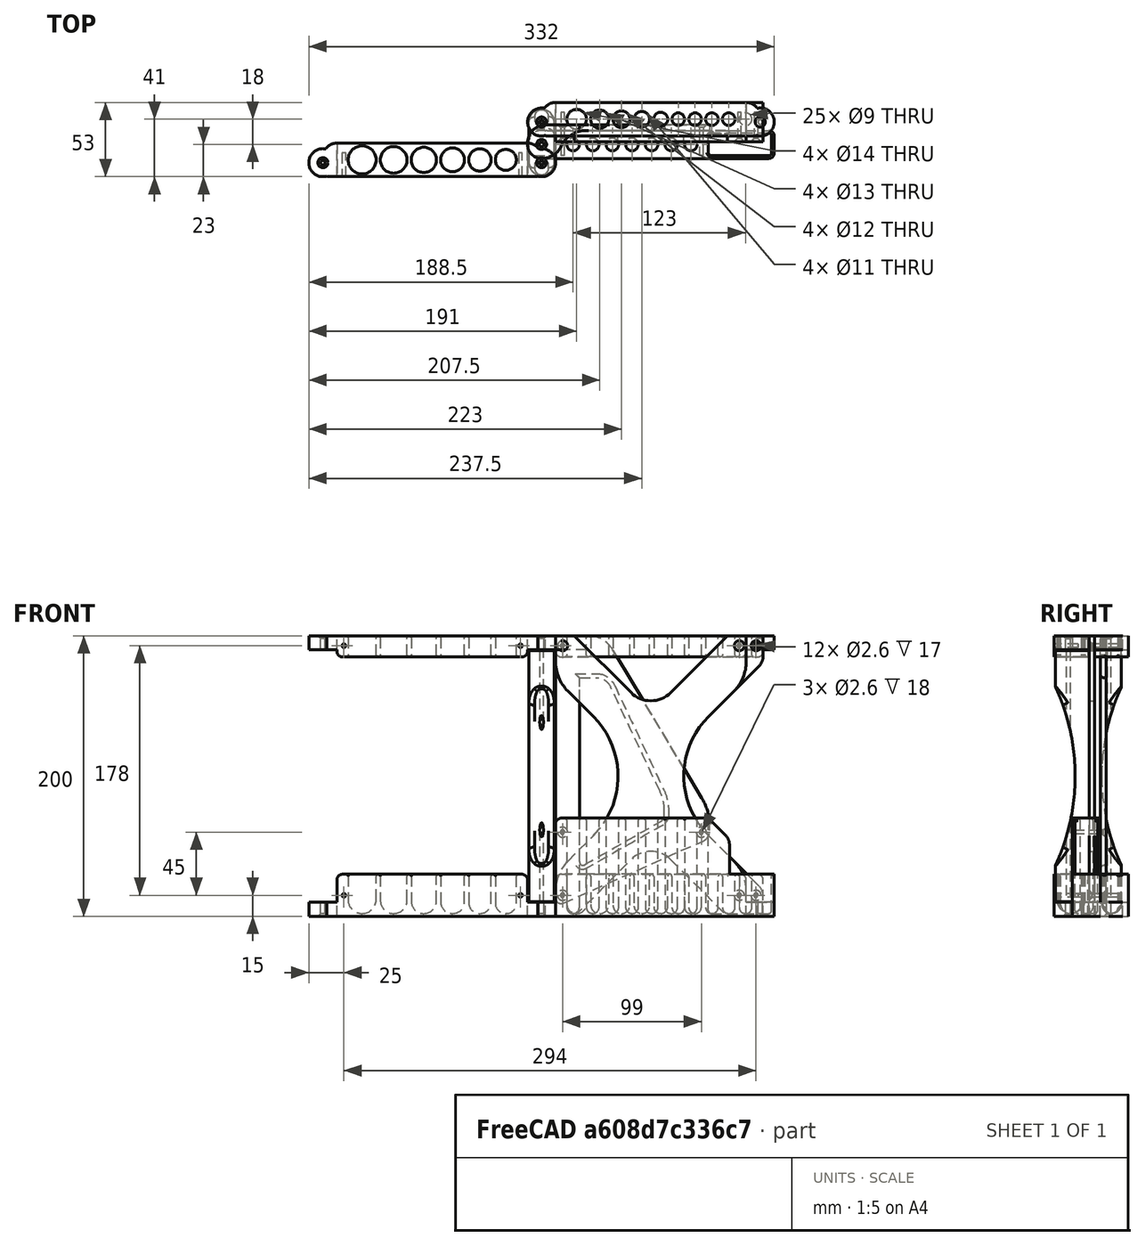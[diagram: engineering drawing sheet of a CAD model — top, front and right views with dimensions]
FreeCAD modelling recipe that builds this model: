
FCSTD DOCUMENT  (FreeCAD 0.21R33771 (Git))
Label: BrushHolder
License: All rights reserved
LicenseURL: https://en.wikipedia.org/wiki/All_rights_reserved
objects: Part::Fillet×106, Part::Cylinder×87, Part::MultiFuse×37, Part::Box×36, Part::Chamfer×24, Part::Cut×17, Part::FeaturePython×12, Part::Feature×1
note: 320 computed .brp shape members not serialized (recipe doc carries the construction recipe); baked Part::Feature solids carry a one-line shape summary decoded from their .brp

FEATURE [Part::Box] Box  label="Cube"
  AttacherType = Attacher::AttachEngine3D
  Height = 30
  Length = 136
  Placement = pos=(-18,-12,0) rot=(0,0,1;0rad)
  Width = 24
FEATURE [Part::Cylinder] Cylinder
  Angle = 360
  AttacherType = Attacher::AttachEngine3D
  FirstAngle = 0
  Height = 30
  Placement = pos=(0,0,2) rot=(0,0,1;0rad)
  Radius = 10
  SecondAngle = 0
FEATURE [Part::Fillet] Fillet
  Base = -> Cylinder
  Edges = 1 edges r=9.9: [Edge2]
FEATURE [Part::Cylinder] Cylinder001
  Angle = 360
  AttacherType = Attacher::AttachEngine3D
  FirstAngle = 0
  Height = 30
  Placement = pos=(22.5,0,2) rot=(0,0,1;0rad)
  Radius = 9.5
  SecondAngle = 0
FEATURE [Part::Fillet] Fillet002
  Base = -> Cylinder001
  Edges = 1 edges r=9.4: [Edge2]
FEATURE [Part::Cylinder] Cylinder002
  Angle = 360
  AttacherType = Attacher::AttachEngine3D
  FirstAngle = 0
  Height = 30
  Placement = pos=(44,0,2) rot=(0,0,1;0rad)
  Radius = 9
  SecondAngle = 0
FEATURE [Part::Fillet] Fillet003
  Base = -> Cylinder002
  Edges = 1 edges r=8.9: [Edge2]
FEATURE [Part::Cylinder] Cylinder003
  Angle = 360
  AttacherType = Attacher::AttachEngine3D
  FirstAngle = 0
  Height = 30
  Placement = pos=(64.5,0,2) rot=(0,0,1;0rad)
  Radius = 8.5
  SecondAngle = 0
FEATURE [Part::Fillet] Fillet004
  Base = -> Cylinder003
  Edges = 1 edges r=8.4: [Edge2]
FEATURE [Part::Cylinder] Cylinder004
  Angle = 360
  AttacherType = Attacher::AttachEngine3D
  FirstAngle = 0
  Height = 30
  Placement = pos=(84,0,2) rot=(0,0,1;0rad)
  Radius = 8
  SecondAngle = 0
FEATURE [Part::Fillet] Fillet005
  Base = -> Cylinder004
  Edges = 1 edges r=7.9: [Edge2]
FEATURE [Part::Cylinder] Cylinder005
  Angle = 360
  AttacherType = Attacher::AttachEngine3D
  FirstAngle = 0
  Height = 30
  Placement = pos=(102.5,0,2) rot=(0,0,1;0rad)
  Radius = 7.5
  SecondAngle = 0
FEATURE [Part::Fillet] Fillet006
  Base = -> Cylinder005
  Edges = 1 edges r=7.4: [Edge2]
FEATURE [Part::MultiFuse] Fusion  label="BrushHolles_001"
  Shapes = -> [Fillet,Fillet002,Fillet003,Fillet004,Fillet005,Fillet006]
FEATURE [Part::Cylinder] Cylinder006
  Angle = 360
  AttacherType = Attacher::AttachEngine3D
  FirstAngle = 0
  Height = 30
  Placement = pos=(-3,0,2) rot=(0,0,1;0rad)
  Radius = 7
  SecondAngle = 0
FEATURE [Part::Fillet] Fillet007
  Base = -> Cylinder006
  Edges = 1 edges r=6.9: [Edge2]
FEATURE [Part::Cylinder] Cylinder007
  Angle = 360
  AttacherType = Attacher::AttachEngine3D
  FirstAngle = 0
  Height = 30
  Placement = pos=(13.5,0,2) rot=(0,0,1;0rad)
  Radius = 6.5
  SecondAngle = 0
FEATURE [Part::Fillet] Fillet008
  Base = -> Cylinder007
  Edges = 1 edges r=6.4: [Edge2]
FEATURE [Part::Cylinder] Cylinder008
  Angle = 360
  AttacherType = Attacher::AttachEngine3D
  FirstAngle = 0
  Height = 30
  Placement = pos=(29,0,2) rot=(0,0,1;0rad)
  Radius = 6
  SecondAngle = 0
FEATURE [Part::Fillet] Fillet009
  Base = -> Cylinder008
  Edges = 1 edges r=5.9: [Edge2]
FEATURE [Part::Cylinder] Cylinder009
  Angle = 360
  AttacherType = Attacher::AttachEngine3D
  FirstAngle = 0
  Height = 30
  Placement = pos=(43.5,0,2) rot=(0,0,1;0rad)
  Radius = 5.5
  SecondAngle = 0
FEATURE [Part::Fillet] Fillet010
  Base = -> Cylinder009
  Edges = 1 edges r=5.4: [Edge2]
FEATURE [Part::Cylinder] Cylinder010
  Angle = 360
  AttacherType = Attacher::AttachEngine3D
  FirstAngle = 0
  Height = 30
  Placement = pos=(57,0,2) rot=(0,0,1;0rad)
  Radius = 5
  SecondAngle = 0
FEATURE [Part::Fillet] Fillet011
  Base = -> Cylinder010
  Edges = 1 edges r=4.9: [Edge2]
FEATURE [Part::Cylinder] Cylinder011
  Angle = 360
  AttacherType = Attacher::AttachEngine3D
  FirstAngle = 0
  Height = 30
  Placement = pos=(69.5,0,2) rot=(0,0,1;0rad)
  Radius = 4.5
  SecondAngle = 0
FEATURE [Part::Fillet] Fillet012
  Base = -> Cylinder011
  Edges = 1 edges r=4.4: [Edge2]
FEATURE [Part::Cylinder] Cylinder012
  Angle = 360
  AttacherType = Attacher::AttachEngine3D
  FirstAngle = 0
  Height = 30
  Placement = pos=(81.5,0,2) rot=(0,0,1;0rad)
  Radius = 4.5
  SecondAngle = 0
FEATURE [Part::Fillet] Fillet013
  Base = -> Cylinder012
  Edges = 1 edges r=4.4: [Edge2]
FEATURE [Part::Cylinder] Cylinder013
  Angle = 360
  AttacherType = Attacher::AttachEngine3D
  FirstAngle = 0
  Height = 30
  Placement = pos=(93.5,0,2) rot=(0,0,1;0rad)
  Radius = 4.5
  SecondAngle = 0
FEATURE [Part::Fillet] Fillet014
  Base = -> Cylinder013
  Edges = 1 edges r=4.4: [Edge2]
FEATURE [Part::Cylinder] Cylinder014
  Angle = 360
  AttacherType = Attacher::AttachEngine3D
  FirstAngle = 0
  Height = 30
  Placement = pos=(105.5,0,2) rot=(0,0,1;0rad)
  Radius = 4.5
  SecondAngle = 0
FEATURE [Part::Fillet] Fillet015
  Base = -> Cylinder014
  Edges = 1 edges r=4.4: [Edge2]
FEATURE [Part::Cut] Cut
  Base = -> Box
  Tool = -> Fusion
FEATURE [Part::Cylinder] Cylinder015  label="ScrewHolle001"
  Angle = 360
  AttacherType = Attacher::AttachEngine3D
  FirstAngle = 0
  Height = 25
  Placement = pos=(-13,-20,15) rot=(-1,0,0;1.5708rad)
  Radius = 1.3
  SecondAngle = 0
FEATURE [Part::MultiFuse] Fusion001  label="BrushHolles_002"
  Shapes = -> [Fillet007,Fillet008,Fillet009,Fillet010,Fillet011,Fillet012,Fillet013,Fillet014,Fillet015]
FEATURE [Part::FeaturePython] Tube  # WARN: FeaturePython — macro-defined, semantics opaque (R4)
  AttacherType = Attacher::AttachEngine3D
  Height = 10
  InnerRadius = 1.6
  OuterRadius = 10
  Placement = pos=(-28,-2,0) rot=(0,0,1;0rad)
FEATURE [Part::Box] Box001  label="Cube001"
  AttacherType = Attacher::AttachEngine3D
  Height = 10
  Length = 10
  Placement = pos=(-26,-12,0) rot=(0,0,1;0rad)
  Width = 24
FEATURE [Part::Fillet] Fillet016
  Base = -> Box001
  Edges = 1 edges r=2: [Edge1]
FEATURE [Part::Chamfer] Chamfer
  Base = -> Fillet016
  Edges = 1 edges r=4: [Edge4]
FEATURE [Part::Fillet] Fillet017
  Base = -> Chamfer
  Edges = 1 edges r=2: [Edge4]
FEATURE [Part::Fillet] Fillet018
  Base = -> Fillet017
  Edges = 1 edges r=10: [Edge19]
FEATURE [Part::FeaturePython] Tube001  # WARN: FeaturePython — macro-defined, semantics opaque (R4)
  AttacherType = Attacher::AttachEngine3D
  Height = 10
  InnerRadius = 1.6
  OuterRadius = 10
  Placement = pos=(128,-2,0) rot=(0,0,1;0rad)
FEATURE [Part::Box] Box002  label="Cube002"
  AttacherType = Attacher::AttachEngine3D
  Height = 10
  Length = 10
  Placement = pos=(116,-12,0) rot=(0,0,1;0rad)
  Width = 24
FEATURE [Part::Fillet] Fillet019
  Base = -> Box002
  Edges = 1 edges r=2: [Edge5]
FEATURE [Part::Chamfer] Chamfer001
  Base = -> Fillet019
  Edges = 1 edges r=4: [Edge4]
FEATURE [Part::Fillet] Fillet020
  Base = -> Chamfer001
  Edges = 1 edges r=2: [Edge4]
FEATURE [Part::Fillet] Fillet021
  Base = -> Fillet020
  Edges = 1 edges r=10: [Edge19]
FEATURE [Part::Fillet] Fillet022
  Base = -> Cut
  Edges = 2 edges r=4: [Edge2,Edge9]
FEATURE [Part::Fillet] Fillet023
  Base = -> Fillet022
  Edges = 6 edges r=1.4: [Edge19,Edge20,Edge21,Edge22,Edge23,Edge24]
FEATURE [Part::MultiFuse] Fusion002  label="Hindges001"
  Shapes = -> [Tube,Fillet018,Fillet021,Tube001]
FEATURE [Part::Cylinder] Cylinder016  label="ScrewHolle002"
  Angle = 360
  AttacherType = Attacher::AttachEngine3D
  FirstAngle = 0
  Height = 25
  Placement = pos=(113,-20,15) rot=(-1,0,0;1.5708rad)
  Radius = 1.3
  SecondAngle = 0
FEATURE [Part::MultiFuse] Fusion003
  Shapes = -> [Cylinder015,Cylinder016]
FEATURE [Part::Cut] Cut001
  Base = -> Fillet023
  Tool = -> Fusion003
FEATURE [Part::Cylinder] Cylinder017  label="ScrewHolle003"
  Angle = 360
  AttacherType = Attacher::AttachEngine3D
  FirstAngle = 0
  Height = 25
  Placement = pos=(-13,-20,15) rot=(-1,0,0;1.5708rad)
  Radius = 1.3
  SecondAngle = 0
FEATURE [Part::Cylinder] Cylinder018  label="ScrewHolle004"
  Angle = 360
  AttacherType = Attacher::AttachEngine3D
  FirstAngle = 0
  Height = 25
  Placement = pos=(113,-20,15) rot=(-1,0,0;1.5708rad)
  Radius = 1.3
  SecondAngle = 0
FEATURE [Part::MultiFuse] Fusion005
  Shapes = -> [Cylinder017,Cylinder018]
FEATURE [Part::Box] Box003  label="Cube003"
  AttacherType = Attacher::AttachEngine3D
  Height = 10
  Length = 10
  Placement = pos=(-26,-12,0) rot=(0,0,1;0rad)
  Width = 24
FEATURE [Part::Box] Box004  label="Cube004"
  AttacherType = Attacher::AttachEngine3D
  Height = 10
  Length = 10
  Placement = pos=(116,-12,0) rot=(0,0,1;0rad)
  Width = 24
FEATURE [Part::Fillet] Fillet024
  Base = -> Box003
  Edges = 1 edges r=2: [Edge1]
FEATURE [Part::Chamfer] Chamfer002
  Base = -> Fillet024
  Edges = 1 edges r=4: [Edge4]
FEATURE [Part::Fillet] Fillet025
  Base = -> Chamfer002
  Edges = 1 edges r=2: [Edge4]
FEATURE [Part::Fillet] Fillet026
  Base = -> Fillet025
  Edges = 1 edges r=10: [Edge19]
FEATURE [Part::Fillet] Fillet027
  Base = -> Box004
  Edges = 1 edges r=2: [Edge5]
FEATURE [Part::Chamfer] Chamfer003
  Base = -> Fillet027
  Edges = 1 edges r=4: [Edge4]
FEATURE [Part::Fillet] Fillet028
  Base = -> Chamfer003
  Edges = 1 edges r=2: [Edge4]
FEATURE [Part::Fillet] Fillet029
  Base = -> Fillet028
  Edges = 1 edges r=10: [Edge19]
FEATURE [Part::FeaturePython] Tube002  # WARN: FeaturePython — macro-defined, semantics opaque (R4)
  AttacherType = Attacher::AttachEngine3D
  Height = 10
  InnerRadius = 1.6
  OuterRadius = 10
  Placement = pos=(-28,-2,0) rot=(0,0,1;0rad)
FEATURE [Part::FeaturePython] Tube003  # WARN: FeaturePython — macro-defined, semantics opaque (R4)
  AttacherType = Attacher::AttachEngine3D
  Height = 10
  InnerRadius = 1.6
  OuterRadius = 10
  Placement = pos=(128,-2,0) rot=(0,0,1;0rad)
FEATURE [Part::MultiFuse] Fusion006  label="Hindges002"
  Shapes = -> [Tube002,Fillet026,Fillet029,Tube003]
FEATURE [Part::Box] Box005  label="Cube005"
  AttacherType = Attacher::AttachEngine3D
  Height = 30
  Length = 136
  Placement = pos=(-18,-12,0) rot=(0,0,1;0rad)
  Width = 24
FEATURE [Part::MultiFuse] Fusion007
  Shapes = -> [Fusion001,Fusion005]
FEATURE [Part::Cut] Cut002
  Base = -> Box005
  Tool = -> Fusion007
FEATURE [Part::Fillet] Fillet030
  Base = -> Cut002
  Edges = 2 edges r=4: [Edge2,Edge11]
FEATURE [Part::Fillet] Fillet031
  Base = -> Fillet030
  Edges = 9 edges r=1.4: [Edge21,Edge22,Edge23,Edge24,Edge25,Edge26,Edge27,Edge28,Edge29]
FEATURE [Part::Cylinder] Cylinder019
  Angle = 360
  AttacherType = Attacher::AttachEngine3D
  FirstAngle = 0
  Height = 30
  Radius = 10
  SecondAngle = 0
FEATURE [Part::Cylinder] Cylinder020
  Angle = 360
  AttacherType = Attacher::AttachEngine3D
  FirstAngle = 0
  Height = 30
  Placement = pos=(22.5,0,0) rot=(0,0,1;0rad)
  Radius = 9.5
  SecondAngle = 0
FEATURE [Part::Cylinder] Cylinder021
  Angle = 360
  AttacherType = Attacher::AttachEngine3D
  FirstAngle = 0
  Height = 30
  Placement = pos=(44,0,0) rot=(0,0,1;0rad)
  Radius = 9
  SecondAngle = 0
FEATURE [Part::Cylinder] Cylinder022
  Angle = 360
  AttacherType = Attacher::AttachEngine3D
  FirstAngle = 0
  Height = 30
  Placement = pos=(64.5,0,0) rot=(0,0,1;0rad)
  Radius = 8.5
  SecondAngle = 0
FEATURE [Part::Cylinder] Cylinder023
  Angle = 360
  AttacherType = Attacher::AttachEngine3D
  FirstAngle = 0
  Height = 30
  Placement = pos=(84,0,0) rot=(0,0,1;0rad)
  Radius = 8
  SecondAngle = 0
FEATURE [Part::Cylinder] Cylinder024
  Angle = 360
  AttacherType = Attacher::AttachEngine3D
  FirstAngle = 0
  Height = 30
  Placement = pos=(102.5,0,0) rot=(0,0,1;0rad)
  Radius = 7.5
  SecondAngle = 0
FEATURE [Part::Box] Box006  label="Cube006"
  AttacherType = Attacher::AttachEngine3D
  Height = 15
  Length = 136
  Placement = pos=(-18,-12,15) rot=(0,0,1;0rad)
  Width = 24
FEATURE [Part::MultiFuse] Fusion009
  Shapes = -> [Cylinder019,Cylinder020,Cylinder021,Cylinder022,Cylinder023,Cylinder024]
FEATURE [Part::Cut] Cut003
  Base = -> Box006
  Tool = -> Fusion009
FEATURE [Part::Box] Box007  label="Cube007"
  AttacherType = Attacher::AttachEngine3D
  Height = 10
  Length = 10
  Placement = pos=(-26,-12,0) rot=(0,0,1;0rad)
  Width = 24
FEATURE [Part::Box] Box008  label="Cube008"
  AttacherType = Attacher::AttachEngine3D
  Height = 10
  Length = 10
  Placement = pos=(116,-12,0) rot=(0,0,1;0rad)
  Width = 24
FEATURE [Part::Fillet] Fillet034
  Base = -> Box007
  Edges = 1 edges r=2: [Edge1]
FEATURE [Part::Chamfer] Chamfer004
  Base = -> Fillet034
  Edges = 1 edges r=4: [Edge4]
FEATURE [Part::Fillet] Fillet035
  Base = -> Chamfer004
  Edges = 1 edges r=2: [Edge4]
FEATURE [Part::Fillet] Fillet036
  Base = -> Fillet035
  Edges = 1 edges r=10: [Edge19]
FEATURE [Part::Fillet] Fillet037
  Base = -> Box008
  Edges = 1 edges r=2: [Edge5]
FEATURE [Part::Chamfer] Chamfer005
  Base = -> Fillet037
  Edges = 1 edges r=4: [Edge4]
FEATURE [Part::Fillet] Fillet038
  Base = -> Chamfer005
  Edges = 1 edges r=2: [Edge4]
FEATURE [Part::Fillet] Fillet039
  Base = -> Fillet038
  Edges = 1 edges r=10: [Edge19]
FEATURE [Part::FeaturePython] Tube004  # WARN: FeaturePython — macro-defined, semantics opaque (R4)
  AttacherType = Attacher::AttachEngine3D
  Height = 10
  InnerRadius = 1.6
  OuterRadius = 10
  Placement = pos=(-28,-2,0) rot=(0,0,1;0rad)
FEATURE [Part::FeaturePython] Tube005  # WARN: FeaturePython — macro-defined, semantics opaque (R4)
  AttacherType = Attacher::AttachEngine3D
  Height = 10
  InnerRadius = 1.6
  OuterRadius = 10
  Placement = pos=(128,-2,0) rot=(0,0,1;0rad)
FEATURE [Part::MultiFuse] Fusion010  label="Hindges003"
  Placement = pos=(0,0,20) rot=(0,0,1;0rad)
  Shapes = -> [Tube004,Fillet036,Fillet039,Tube005]
FEATURE [Part::Fillet] Fillet040
  Base = -> Cut003
  Edges = 2 edges r=4: [Edge4,Edge18]
FEATURE [Part::Fillet] Fillet041
  Base = -> Fillet040
  Edges = 12 edges r=1.4: [Edge14,Edge15,Edge16,Edge17,Edge18,Edge19,Edge24,Edge25,Edge26,Edge27,Edge28,Edge29]
FEATURE [Part::Chamfer] Chamfer006
  Base = -> Fusion010
  Edges = 2 edges r=2: [Edge31,Edge69]
FEATURE [Part::Cylinder] Cylinder025  label="ScrewHolle005"
  Angle = 360
  AttacherType = Attacher::AttachEngine3D
  FirstAngle = 0
  Height = 25
  Placement = pos=(-13,-20,23) rot=(-1,0,0;1.5708rad)
  Radius = 1.3
  SecondAngle = 0
FEATURE [Part::Cylinder] Cylinder026  label="ScrewHolle006"
  Angle = 360
  AttacherType = Attacher::AttachEngine3D
  FirstAngle = 0
  Height = 25
  Placement = pos=(113,-20,23) rot=(-1,0,0;1.5708rad)
  Radius = 1.3
  SecondAngle = 0
FEATURE [Part::MultiFuse] Fusion011
  Shapes = -> [Cylinder025,Cylinder026]
FEATURE [Part::Cut] Cut004
  Base = -> Fillet041
  Tool = -> Fusion011
FEATURE [Part::MultiFuse] Fusion012  label="Top_L"
  Placement = pos=(-156,-13,170) rot=(0,0,1;0rad)
  Shapes = -> [Cut004,Chamfer006]
FEATURE [Part::Chamfer] Chamfer007
  Base = -> Fusion002
  Edges = 2 edges r=2: [Edge14,Edge74]
FEATURE [Part::MultiFuse] Fusion013  label="BrushHolles_L"
  Placement = pos=(-156,-13,0) rot=(0,0,1;0rad)
  Shapes = -> [Chamfer007,Cut001]
FEATURE [Part::Box] Box010  label="Cube010"
  AttacherType = Attacher::AttachEngine3D
  Height = 10
  Length = 42
  Placement = pos=(-38,-12,190) rot=(0,0,1;0rad)
  Width = 24
FEATURE [Part::Chamfer] Chamfer011
  Base = -> Fusion006
  Edges = 2 edges r=2: [Edge14,Edge74]
FEATURE [Part::MultiFuse] Fusion018  label="BrushHolles_S"
  Placement = pos=(0,16,0) rot=(0,0,1;0rad)
  Shapes = -> [Chamfer011,Fillet031]
FEATURE [Part::Cylinder] Cylinder038  label="ScrewHolle009"
  Angle = 360
  AttacherType = Attacher::AttachEngine3D
  FirstAngle = 0
  Height = 25
  Placement = pos=(-13,-20,15) rot=(-1,0,0;1.5708rad)
  Radius = 1.6
  SecondAngle = 0
FEATURE [Part::Cylinder] Cylinder039  label="ScrewHolle010"
  Angle = 360
  AttacherType = Attacher::AttachEngine3D
  FirstAngle = 0
  Height = 25
  Placement = pos=(113,-20,15) rot=(-1,0,0;1.5708rad)
  Radius = 1.6
  SecondAngle = 0
FEATURE [Part::Cylinder] Cylinder040  label="ScrewHolle011"
  Angle = 360
  AttacherType = Attacher::AttachEngine3D
  FirstAngle = 0
  Height = 25
  Placement = pos=(-13,-20,193) rot=(-1,0,0;1.5708rad)
  Radius = 1.6
  SecondAngle = 0
FEATURE [Part::Cylinder] Cylinder041  label="ScrewHolle012"
  Angle = 360
  AttacherType = Attacher::AttachEngine3D
  FirstAngle = 0
  Height = 25
  Placement = pos=(113,-20,193) rot=(-1,0,0;1.5708rad)
  Radius = 1.6
  SecondAngle = 0
FEATURE [Part::MultiFuse] Fusion019  label="ScrewHolles"
  Shapes = -> [Cylinder038,Cylinder039,Cylinder040,Cylinder041]
FEATURE [Part::Box] Box013  label="Cube013"
  AttacherType = Attacher::AttachEngine3D
  Height = 80
  Length = 80
  Placement = pos=(-6.57,0,202) rot=(0,1,0;0.785398rad)
  Width = 4
FEATURE [Part::Box] Box014  label="Cube014"
  AttacherType = Attacher::AttachEngine3D
  Height = 100
  Length = 100
  Placement = pos=(-90,0,100) rot=(0,1,0;0.785398rad)
  Width = 4
FEATURE [Part::Box] Box015  label="Cube015"
  AttacherType = Attacher::AttachEngine3D
  Height = 179.2
  Length = 18
  Placement = pos=(-37,-24,10.4) rot=(0,0,1;0rad)
  Width = 47
FEATURE [Part::Fillet] Fillet054
  Base = -> Box015
  Edges = 4 edges r=8.9: [Edge1,Edge3,Edge5,Edge7]
FEATURE [Part::Cylinder] Cylinder042
  Angle = 360
  AttacherType = Attacher::AttachEngine3D
  FirstAngle = 0
  Height = 190
  Placement = pos=(-28,14,10) rot=(0,0,1;0rad)
  Radius = 1.3
  SecondAngle = 0
FEATURE [Part::Cylinder] Cylinder043
  Angle = 360
  AttacherType = Attacher::AttachEngine3D
  FirstAngle = 0
  Height = 190
  Placement = pos=(-28,-15,10) rot=(0,0,1;0rad)
  Radius = 1.3
  SecondAngle = 0
FEATURE [Part::Box] Box016  label="Cube016"
  AttacherType = Attacher::AttachEngine3D
  Height = 140
  Length = 20
  Placement = pos=(-38,0,30) rot=(0,0,1;0rad)
  Width = 47
FEATURE [Part::Chamfer] Chamfer015
  Base = -> Box016
  Edges = 2 edges r=20: [Edge11,Edge12]
FEATURE [Part::Chamfer] Chamfer016
  Base = -> Chamfer015
  Edges = 2 edges r=20: [Edge10,Edge15]
FEATURE [Part::Fillet] Fillet055
  Base = -> Chamfer016
  Edges = 2 edges r=20: [Edge9,Edge20]
FEATURE [Part::Fillet] Fillet056
  Base = -> Fillet055
  Edges = 2 edges r=8: [Edge13,Edge25]
FEATURE [Part::Fillet] Fillet057  label="Hollow005"
  Base = -> Fillet056
  Edges = 2 edges r=150: [Edge22,Edge27]
  Placement = pos=(0,-57,0) rot=(0,0,1;0rad)
FEATURE [Part::Feature] Part__Mirroring003  label="Hollow006"
  Placement = pos=(0,2,0) rot=(0,0,1;0rad)
  shape: bbox 20 x 47 x 140 mm, 16 faces (baked)
FEATURE [Part::MultiFuse] Fusion021
  Shapes = -> [Part__Mirroring003,Fillet057,Cylinder043,Cylinder042]
FEATURE [Part::Cut] Cut007
  Base = -> Fillet054
  Tool = -> Fusion021
FEATURE [Part::Fillet] Fillet058  label="MainHindge"
  Base = -> Cut007
  Edges = 2 edges r=4: [Edge3,Edge11]
FEATURE [Part::Fillet] Fillet059
  Base = -> Box013
  Edges = 1 edges r=20: [Edge8]
FEATURE [Part::Box] Box017  label="Cube017"
  AttacherType = Attacher::AttachEngine3D
  Height = 80
  Length = 80
  Placement = pos=(-6.57,0,-2) rot=(0,1,0;0.785398rad)
  Width = 4
FEATURE [Part::Fillet] Fillet060
  Base = -> Box017
  Edges = 1 edges r=20: [Edge2]
FEATURE [Part::Box] Box012  label="SupportBase"
  AttacherType = Attacher::AttachEngine3D
  Height = 200
  Length = 136
  Placement = pos=(-18,0,0) rot=(0,0,1;0rad)
  Width = 4
FEATURE [Part::Fillet] Fillet061
  Base = -> Box014
  Edges = 1 edges r=60: [Edge6]
FEATURE [Part::Box] Box018  label="Cube018"
  AttacherType = Attacher::AttachEngine3D
  Height = 100
  Length = 100
  Placement = pos=(48.67,0,100) rot=(0,1,0;0.785398rad)
  Width = 4
FEATURE [Part::Fillet] Fillet062
  Base = -> Box018
  Edges = 1 edges r=60: [Edge4]
FEATURE [Part::MultiFuse] Fusion023
  Shapes = -> [Fillet061,Fillet059,Fillet060,Fillet062,Fusion019]
FEATURE [Part::Cut] Cut008
  Base = -> Box012
  Tool = -> Fusion023
FEATURE [Part::Fillet] Fillet063
  Base = -> Cut008
  Edges = 4 edges r=30: [Edge2,Edge57,Edge60,Edge67]
FEATURE [Part::Chamfer] Chamfer017  label="Support"
  Base = -> Fillet063
  Edges = 4 edges r=2: [Edge28,Edge29,Edge30,Edge31]
FEATURE [Part::Box] Box019  label="Cube019"
  AttacherType = Attacher::AttachEngine3D
  Height = 10
  Length = 10
  Placement = pos=(-26,-12,0) rot=(0,0,1;0rad)
  Width = 20
FEATURE [Part::Box] Box021  label="Cube021"
  AttacherType = Attacher::AttachEngine3D
  Height = 30
  Length = 88
  Placement = pos=(50,-12,0) rot=(0,0,1;0rad)
  Width = 20
FEATURE [Part::Cylinder] Cylinder049 .. Cylinder052  x4 (patterned run collapsed; names and placements below)
  Angle = 360
  AttacherType = Attacher::AttachEngine3D
  FirstAngle = 0
  Height = 120
  Radius = 4.5
  SecondAngle = 0
  placements: 4 in arithmetic series — first pos=(8.5,-2,2) rot=(0,0,1;0rad), step (14,0,0), last pos=(50.5,-2,2) rot=(0,0,1;0rad)
FEATURE [Part::Cylinder] Cylinder053  label="ScrewHolle013"
  Angle = 360
  AttacherType = Attacher::AttachEngine3D
  FirstAngle = 0
  Height = 25
  Placement = pos=(-13,-10,15) rot=(-1,0,0;1.5708rad)
  Radius = 1.3
  SecondAngle = 0
FEATURE [Part::Cylinder] Cylinder054  label="ScrewHolle014"
  Angle = 360
  AttacherType = Attacher::AttachEngine3D
  FirstAngle = 0
  Height = 25
  Placement = pos=(86,-10,60) rot=(-1,0,0;1.5708rad)
  Radius = 1.3
  SecondAngle = 0
FEATURE [Part::Fillet] Fillet069
  Base = -> Cylinder049
  Edges = 1 edges r=4.4: [Edge2]
FEATURE [Part::Fillet] Fillet070
  Base = -> Cylinder050
  Edges = 1 edges r=4.4: [Edge2]
FEATURE [Part::Fillet] Fillet071
  Base = -> Cylinder051
  Edges = 1 edges r=4.4: [Edge2]
FEATURE [Part::Fillet] Fillet072
  Base = -> Cylinder052
  Edges = 1 edges r=4.4: [Edge2]
FEATURE [Part::Fillet] Fillet073
  Base = -> Box019
  Edges = 2 edges r=2: [Edge1,Edge3]
FEATURE [Part::FeaturePython] Tube008  # WARN: FeaturePython — macro-defined, semantics opaque (R4)
  AttacherType = Attacher::AttachEngine3D
  Height = 10
  InnerRadius = 1.6
  OuterRadius = 10
  Placement = pos=(-28,-2,0) rot=(0,0,1;0rad)
FEATURE [Part::Cylinder] Cylinder055
  Angle = 360
  AttacherType = Attacher::AttachEngine3D
  FirstAngle = 0
  Height = 120
  Placement = pos=(-5.5,-2,2) rot=(0,0,1;0rad)
  Radius = 4.5
  SecondAngle = 0
FEATURE [Part::Fillet] Fillet079
  Base = -> Cylinder055
  Edges = 1 edges r=4.4: [Edge2]
FEATURE [Part::Box] Box022  label="Cube022"
  AttacherType = Attacher::AttachEngine3D
  Height = 120
  Length = 45
  Placement = pos=(91,-10,2) rot=(0,0,1;0rad)
  Width = 16
FEATURE [Part::Fillet] Fillet081
  Base = -> Box022
  Edges = 4 edges r=2: [Edge1,Edge3,Edge5,Edge7]
FEATURE [Part::Fillet] Fillet082
  Base = -> Fillet081
  Edges = 1 edges r=2: [Edge16]
FEATURE [Part::Box] Box024  label="Cube024"
  AttacherType = Attacher::AttachEngine3D
  Height = 70
  Length = 124
  Placement = pos=(-18,-12,0) rot=(0,0,1;0rad)
  Width = 20
FEATURE [Part::Fillet] Fillet085
  Base = -> Box021
  Edges = 2 edges r=4: [Edge5,Edge7]
FEATURE [Part::Cylinder] Cylinder056
  Angle = 360
  AttacherType = Attacher::AttachEngine3D
  FirstAngle = 0
  Height = 10
  Placement = pos=(-28,-2,190) rot=(0,0,1;0rad)
  Radius = 1.6
  SecondAngle = 0
FEATURE [Part::Box] Box025  label="Cube025"
  AttacherType = Attacher::AttachEngine3D
  Height = 200
  Length = 110
  Placement = pos=(-18,8,0) rot=(0,0,1;0rad)
  Width = 4
FEATURE [Part::Cylinder] Cylinder060  label="ScrewHolle018"
  Angle = 360
  AttacherType = Attacher::AttachEngine3D
  FirstAngle = 0
  Height = 25
  Placement = pos=(-13,-10,60) rot=(-1,0,0;1.5708rad)
  Radius = 1.3
  SecondAngle = 0
FEATURE [Part::MultiFuse] Fusion035
  Shapes = -> [Fillet073,Tube008]
FEATURE [Part::Chamfer] Chamfer026
  Base = -> Fusion035
  Edges = 1 edges r=2: [Edge17]
FEATURE [Part::Cylinder] Cylinder061  label="ScrewHolle019"
  Angle = 360
  AttacherType = Attacher::AttachEngine3D
  FirstAngle = 0
  Height = 25
  Placement = pos=(-13,-10,15) rot=(-1,0,0;1.5708rad)
  Radius = 1.6
  SecondAngle = 0
FEATURE [Part::Cylinder] Cylinder062  label="ScrewHolle020"
  Angle = 360
  AttacherType = Attacher::AttachEngine3D
  FirstAngle = 0
  Height = 25
  Placement = pos=(-13,-10,60) rot=(-1,0,0;1.5708rad)
  Radius = 1.6
  SecondAngle = 0
FEATURE [Part::Cylinder] Cylinder063  label="ScrewHolle021"
  Angle = 360
  AttacherType = Attacher::AttachEngine3D
  FirstAngle = 0
  Height = 25
  Placement = pos=(86,-10,60) rot=(-1,0,0;1.5708rad)
  Radius = 1.6
  SecondAngle = 0
FEATURE [Part::Cylinder] Cylinder064
  Angle = 360
  AttacherType = Attacher::AttachEngine3D
  FirstAngle = 0
  Height = 10
  Placement = pos=(4,-12,190) rot=(0,0,1;0rad)
  Radius = 20
  SecondAngle = 0
FEATURE [Part::Box] Box026  label="Cube026"
  AttacherType = Attacher::AttachEngine3D
  Height = 10
  Length = 10
  Placement = pos=(-26,-12,0) rot=(0,0,1;0rad)
  Width = 24
FEATURE [Part::Box] Box028  label="Cube028"
  AttacherType = Attacher::AttachEngine3D
  Height = 30
  Length = 148
  Placement = pos=(-18,-12,0) rot=(0,0,1;0rad)
  Width = 24
FEATURE [Part::Cylinder] Cylinder065
  Angle = 360
  AttacherType = Attacher::AttachEngine3D
  FirstAngle = 0
  Height = 30
  Placement = pos=(-3,0,2) rot=(0,0,1;0rad)
  Radius = 7
  SecondAngle = 0
FEATURE [Part::Cylinder] Cylinder066
  Angle = 360
  AttacherType = Attacher::AttachEngine3D
  FirstAngle = 0
  Height = 30
  Placement = pos=(13.5,0,2) rot=(0,0,1;0rad)
  Radius = 6.5
  SecondAngle = 0
FEATURE [Part::Cylinder] Cylinder067
  Angle = 360
  AttacherType = Attacher::AttachEngine3D
  FirstAngle = 0
  Height = 30
  Placement = pos=(29,0,2) rot=(0,0,1;0rad)
  Radius = 6
  SecondAngle = 0
FEATURE [Part::Cylinder] Cylinder068
  Angle = 360
  AttacherType = Attacher::AttachEngine3D
  FirstAngle = 0
  Height = 30
  Placement = pos=(43.5,0,2) rot=(0,0,1;0rad)
  Radius = 5.5
  SecondAngle = 0
FEATURE [Part::Cylinder] Cylinder069
  Angle = 360
  AttacherType = Attacher::AttachEngine3D
  FirstAngle = 0
  Height = 30
  Placement = pos=(57,0,2) rot=(0,0,1;0rad)
  Radius = 5
  SecondAngle = 0
FEATURE [Part::Cylinder] Cylinder070 .. Cylinder073  x4 (patterned run collapsed; names and placements below)
  Angle = 360
  AttacherType = Attacher::AttachEngine3D
  FirstAngle = 0
  Height = 30
  Radius = 4.5
  SecondAngle = 0
  placements: 4 in arithmetic series — first pos=(69.5,0,2) rot=(0,0,1;0rad), step (12,0,0), last pos=(105.5,0,2) rot=(0,0,1;0rad)
FEATURE [Part::Cylinder] Cylinder074  label="ScrewHolle022"
  Angle = 360
  AttacherType = Attacher::AttachEngine3D
  FirstAngle = 0
  Height = 25
  Placement = pos=(-13,-20,15) rot=(-1,0,0;1.5708rad)
  Radius = 1.3
  SecondAngle = 0
FEATURE [Part::Cylinder] Cylinder075  label="ScrewHolle023"
  Angle = 360
  AttacherType = Attacher::AttachEngine3D
  FirstAngle = 0
  Height = 25
  Placement = pos=(125,-20,15) rot=(-1,0,0;1.5708rad)
  Radius = 1.3
  SecondAngle = 0
FEATURE [Part::Fillet] Fillet109  label="Fillet110"
  Base = -> Cylinder065
  Edges = 1 edges r=6.9: [Edge2]
FEATURE [Part::Fillet] Fillet110  label="Fillet111"
  Base = -> Cylinder066
  Edges = 1 edges r=6.4: [Edge2]
FEATURE [Part::Fillet] Fillet111  label="Fillet112"
  Base = -> Cylinder067
  Edges = 1 edges r=5.9: [Edge2]
FEATURE [Part::Fillet] Fillet112  label="Fillet113"
  Base = -> Cylinder068
  Edges = 1 edges r=5.4: [Edge2]
FEATURE [Part::Fillet] Fillet113  label="Fillet114"
  Base = -> Cylinder069
  Edges = 1 edges r=4.9: [Edge2]
FEATURE [Part::Fillet] Fillet114  label="Fillet115"
  Base = -> Cylinder070
  Edges = 1 edges r=4.4: [Edge2]
FEATURE [Part::Fillet] Fillet115  label="Fillet116"
  Base = -> Cylinder071
  Edges = 1 edges r=4.4: [Edge2]
FEATURE [Part::Fillet] Fillet116  label="Fillet117"
  Base = -> Cylinder072
  Edges = 1 edges r=4.4: [Edge2]
FEATURE [Part::Fillet] Fillet117  label="Fillet118"
  Base = -> Cylinder073
  Edges = 1 edges r=4.4: [Edge2]
FEATURE [Part::Fillet] Fillet118  label="Fillet119"
  Base = -> Box026
  Edges = 1 edges r=2: [Edge1]
FEATURE [Part::MultiFuse] Fusion043
  Shapes = -> [Cylinder074,Cylinder075]
FEATURE [Part::FeaturePython] Tube009  # WARN: FeaturePython — macro-defined, semantics opaque (R4)
  AttacherType = Attacher::AttachEngine3D
  Height = 10
  InnerRadius = 1.6
  OuterRadius = 10
  Placement = pos=(-28,-2,0) rot=(0,0,1;0rad)
FEATURE [Part::Cylinder] Cylinder076
  Angle = 360
  AttacherType = Attacher::AttachEngine3D
  FirstAngle = 0
  Height = 30
  Placement = pos=(117.5,0,2) rot=(0,0,1;0rad)
  Radius = 4.5
  SecondAngle = 0
FEATURE [Part::Fillet] Fillet122  label="Fillet123"
  Base = -> Cylinder076
  Edges = 1 edges r=4.4: [Edge2]
FEATURE [Part::Fillet] Fillet123  label="Fillet124"
  Base = -> Box028
  Edges = 2 edges r=4: [Edge2,Edge6]
FEATURE [Part::MultiFuse] Fusion047
  Shapes = -> [Fillet122,Fillet117,Fillet116,Fillet115,Fillet114,Fillet113,Fillet112,Fillet111,Fillet110,Fillet109,Fusion043]
FEATURE [Part::Cut] Cut015
  Base = -> Fillet123
  Tool = -> Fusion047
FEATURE [Part::Fillet] Fillet124  label="Fillet125"
  Base = -> Cut015
  Edges = 10 edges r=1.4: [Edge21,Edge22,Edge23,Edge24,Edge25,Edge26,Edge27,Edge28,Edge29,Edge30]
FEATURE [Part::Chamfer] Chamfer031
  Base = -> Fillet118
  Edges = 1 edges r=4: [Edge4]
FEATURE [Part::Fillet] Fillet119  label="Fillet120"
  Base = -> Chamfer031
  Edges = 1 edges r=2: [Edge4]
FEATURE [Part::Fillet] Fillet120  label="Fillet121"
  Base = -> Fillet119
  Edges = 1 edges r=10: [Edge19]
FEATURE [Part::MultiFuse] Fusion046
  Shapes = -> [Fillet120,Tube009]
FEATURE [Part::Chamfer] Chamfer032
  Base = -> Fusion046
  Edges = 1 edges r=2: [Edge36]
FEATURE [Part::MultiFuse] Fusion048  label="BrushHolles_S2"
  Placement = pos=(0,16,0) rot=(0,0,1;0rad)
  Shapes = -> [Fillet124,Chamfer032]
FEATURE [Part::Box] Box009  label="Cube009"
  AttacherType = Attacher::AttachEngine3D
  Height = 15
  Length = 136
  Placement = pos=(-18,-12,15) rot=(0,0,1;0rad)
  Width = 24
FEATURE [Part::Box] Box029  label="Cube029"
  AttacherType = Attacher::AttachEngine3D
  Height = 10
  Length = 10
  Placement = pos=(-26,-12,0) rot=(0,0,1;0rad)
  Width = 24
FEATURE [Part::Box] Box011  label="Cube011"
  AttacherType = Attacher::AttachEngine3D
  Height = 10
  Length = 10
  Placement = pos=(116,-12,0) rot=(0,0,1;0rad)
  Width = 24
FEATURE [Part::Cylinder] Cylinder027
  Angle = 360
  AttacherType = Attacher::AttachEngine3D
  FirstAngle = 0
  Height = 30
  Placement = pos=(-3,0,0) rot=(0,0,1;0rad)
  Radius = 7
  SecondAngle = 0
FEATURE [Part::Cylinder] Cylinder028
  Angle = 360
  AttacherType = Attacher::AttachEngine3D
  FirstAngle = 0
  Height = 30
  Placement = pos=(13.5,0,0) rot=(0,0,1;0rad)
  Radius = 6.5
  SecondAngle = 0
FEATURE [Part::Cylinder] Cylinder029
  Angle = 360
  AttacherType = Attacher::AttachEngine3D
  FirstAngle = 0
  Height = 30
  Placement = pos=(29,0,0) rot=(0,0,1;0rad)
  Radius = 6
  SecondAngle = 0
FEATURE [Part::Cylinder] Cylinder030
  Angle = 360
  AttacherType = Attacher::AttachEngine3D
  FirstAngle = 0
  Height = 30
  Placement = pos=(43.5,0,0) rot=(0,0,1;0rad)
  Radius = 5.5
  SecondAngle = 0
FEATURE [Part::Cylinder] Cylinder031
  Angle = 360
  AttacherType = Attacher::AttachEngine3D
  FirstAngle = 0
  Height = 30
  Placement = pos=(57,0,0) rot=(0,0,1;0rad)
  Radius = 5
  SecondAngle = 0
FEATURE [Part::Cylinder] Cylinder032 .. Cylinder035  x4 (patterned run collapsed; names and placements below)
  Angle = 360
  AttacherType = Attacher::AttachEngine3D
  FirstAngle = 0
  Height = 30
  Radius = 4.5
  SecondAngle = 0
  placements: 4 in arithmetic series — first pos=(69.5,0,0) rot=(0,0,1;0rad), step (12,0,0), last pos=(105.5,0,0) rot=(0,0,1;0rad)
FEATURE [Part::Cylinder] Cylinder036  label="ScrewHolle007"
  Angle = 360
  AttacherType = Attacher::AttachEngine3D
  FirstAngle = 0
  Height = 25
  Placement = pos=(-13,-20,23) rot=(-1,0,0;1.5708rad)
  Radius = 1.3
  SecondAngle = 0
FEATURE [Part::Cylinder] Cylinder037  label="ScrewHolle008"
  Angle = 360
  AttacherType = Attacher::AttachEngine3D
  FirstAngle = 0
  Height = 25
  Placement = pos=(113,-20,23) rot=(-1,0,0;1.5708rad)
  Radius = 1.3
  SecondAngle = 0
FEATURE [Part::Fillet] Fillet042
  Base = -> Box029
  Edges = 1 edges r=2: [Edge1]
FEATURE [Part::Chamfer] Chamfer008
  Base = -> Fillet042
  Edges = 1 edges r=4: [Edge4]
FEATURE [Part::Fillet] Fillet043
  Base = -> Chamfer008
  Edges = 1 edges r=2: [Edge4]
FEATURE [Part::Fillet] Fillet044
  Base = -> Fillet043
  Edges = 1 edges r=10: [Edge19]
FEATURE [Part::Fillet] Fillet045
  Base = -> Box011
  Edges = 1 edges r=2: [Edge5]
FEATURE [Part::Chamfer] Chamfer009
  Base = -> Fillet045
  Edges = 1 edges r=4: [Edge4]
FEATURE [Part::Fillet] Fillet046
  Base = -> Chamfer009
  Edges = 1 edges r=2: [Edge4]
FEATURE [Part::Fillet] Fillet047
  Base = -> Fillet046
  Edges = 1 edges r=10: [Edge19]
FEATURE [Part::MultiFuse] Fusion015
  Shapes = -> [Cylinder036,Cylinder037]
FEATURE [Part::MultiFuse] Fusion016
  Shapes = -> [Cylinder027,Cylinder028,Cylinder029,Cylinder030,Cylinder031,Cylinder032,Cylinder033,Cylinder034,Cylinder035,Fusion015]
FEATURE [Part::Cut] Cut005
  Base = -> Box009
  Tool = -> Fusion016
FEATURE [Part::Fillet] Fillet048
  Base = -> Cut005
  Edges = 2 edges r=4: [Edge4,Edge23]
FEATURE [Part::Fillet] Fillet049
  Base = -> Fillet048
  Edges = 18 edges r=1.4: [Edge16,Edge17,Edge18,Edge19,Edge20,Edge21,Edge22,Edge23,Edge24,Edge29,Edge30,Edge31,Edge32,Edge33,Edge34,Edge35,Edge36,Edge37]
FEATURE [Part::FeaturePython] Tube006  # WARN: FeaturePython — macro-defined, semantics opaque (R4)
  AttacherType = Attacher::AttachEngine3D
  Height = 10
  InnerRadius = 1.6
  OuterRadius = 10
  Placement = pos=(-28,-2,0) rot=(0,0,1;0rad)
FEATURE [Part::FeaturePython] Tube007  # WARN: FeaturePython — macro-defined, semantics opaque (R4)
  AttacherType = Attacher::AttachEngine3D
  Height = 10
  InnerRadius = 1.6
  OuterRadius = 10
  Placement = pos=(128,-2,0) rot=(0,0,1;0rad)
FEATURE [Part::MultiFuse] Fusion014  label="Hindges004"
  Placement = pos=(0,0,20) rot=(0,0,1;0rad)
  Shapes = -> [Tube006,Fillet044,Fillet047,Tube007]
FEATURE [Part::Chamfer] Chamfer010
  Base = -> Fusion014
  Edges = 2 edges r=2: [Edge31,Edge69]
FEATURE [Part::MultiFuse] Fusion022  label="Top_S"
  Placement = pos=(0,16,170) rot=(0,0,1;0rad)
  Shapes = -> [Fillet049,Chamfer010]
FEATURE [Part::Box] Box030  label="Cube030"
  AttacherType = Attacher::AttachEngine3D
  Height = 15
  Length = 148
  Placement = pos=(-18,-12,15) rot=(0,0,1;0rad)
  Width = 24
FEATURE [Part::Box] Box031  label="Cube031"
  AttacherType = Attacher::AttachEngine3D
  Height = 10
  Length = 10
  Placement = pos=(-26,-12,20) rot=(0,0,1;0rad)
  Width = 24
FEATURE [Part::Cylinder] Cylinder077
  Angle = 360
  AttacherType = Attacher::AttachEngine3D
  FirstAngle = 0
  Height = 30
  Placement = pos=(-3,0,0) rot=(0,0,1;0rad)
  Radius = 7
  SecondAngle = 0
FEATURE [Part::Cylinder] Cylinder078
  Angle = 360
  AttacherType = Attacher::AttachEngine3D
  FirstAngle = 0
  Height = 30
  Placement = pos=(13.5,0,0) rot=(0,0,1;0rad)
  Radius = 6.5
  SecondAngle = 0
FEATURE [Part::Cylinder] Cylinder079
  Angle = 360
  AttacherType = Attacher::AttachEngine3D
  FirstAngle = 0
  Height = 30
  Placement = pos=(29,0,0) rot=(0,0,1;0rad)
  Radius = 6
  SecondAngle = 0
FEATURE [Part::Cylinder] Cylinder080
  Angle = 360
  AttacherType = Attacher::AttachEngine3D
  FirstAngle = 0
  Height = 30
  Placement = pos=(43.5,0,0) rot=(0,0,1;0rad)
  Radius = 5.5
  SecondAngle = 0
FEATURE [Part::Cylinder] Cylinder081
  Angle = 360
  AttacherType = Attacher::AttachEngine3D
  FirstAngle = 0
  Height = 30
  Placement = pos=(57,0,0) rot=(0,0,1;0rad)
  Radius = 5
  SecondAngle = 0
FEATURE [Part::Cylinder] Cylinder082 .. Cylinder085  x4 (patterned run collapsed; names and placements below)
  Angle = 360
  AttacherType = Attacher::AttachEngine3D
  FirstAngle = 0
  Height = 30
  Radius = 4.5
  SecondAngle = 0
  placements: 4 in arithmetic series — first pos=(69.5,0,0) rot=(0,0,1;0rad), step (12,0,0), last pos=(105.5,0,0) rot=(0,0,1;0rad)
FEATURE [Part::Cylinder] Cylinder086  label="ScrewHolle024"
  Angle = 360
  AttacherType = Attacher::AttachEngine3D
  FirstAngle = 0
  Height = 25
  Placement = pos=(-13,-20,23) rot=(-1,0,0;1.5708rad)
  Radius = 1.3
  SecondAngle = 0
FEATURE [Part::Cylinder] Cylinder087  label="ScrewHolle025"
  Angle = 360
  AttacherType = Attacher::AttachEngine3D
  FirstAngle = 0
  Height = 25
  Placement = pos=(125,-20,23) rot=(-1,0,0;1.5708rad)
  Radius = 1.3
  SecondAngle = 0
FEATURE [Part::Fillet] Fillet125  label="Fillet126"
  Base = -> Box031
  Edges = 1 edges r=2: [Edge1]
FEATURE [Part::Chamfer] Chamfer033
  Base = -> Fillet125
  Edges = 1 edges r=4: [Edge4]
FEATURE [Part::Fillet] Fillet126  label="Fillet127"
  Base = -> Chamfer033
  Edges = 1 edges r=2: [Edge4]
FEATURE [Part::Fillet] Fillet127  label="Fillet128"
  Base = -> Fillet126
  Edges = 1 edges r=10: [Edge19]
FEATURE [Part::MultiFuse] Fusion050
  Shapes = -> [Cylinder086,Cylinder087]
FEATURE [Part::FeaturePython] Tube010  # WARN: FeaturePython — macro-defined, semantics opaque (R4)
  AttacherType = Attacher::AttachEngine3D
  Height = 10
  InnerRadius = 1.6
  OuterRadius = 10
  Placement = pos=(-28,-2,20) rot=(0,0,1;0rad)
FEATURE [Part::MultiFuse] Fusion052
  Shapes = -> [Fillet127,Tube010]
FEATURE [Part::Chamfer] Chamfer034
  Base = -> Fusion052
  Edges = 1 edges r=2: [Edge32]
FEATURE [Part::Cylinder] Cylinder088
  Angle = 360
  AttacherType = Attacher::AttachEngine3D
  FirstAngle = 0
  Height = 30
  Placement = pos=(117.5,0,0) rot=(0,0,1;0rad)
  Radius = 4.5
  SecondAngle = 0
FEATURE [Part::Fillet] Fillet128  label="Fillet129"
  Base = -> Box030
  Edges = 2 edges r=4: [Edge4,Edge8]
FEATURE [Part::MultiFuse] Fusion053
  Shapes = -> [Fusion050,Cylinder088,Cylinder085,Cylinder084,Cylinder083,Cylinder082,Cylinder081,Cylinder080,Cylinder079,Cylinder078,Cylinder077]
FEATURE [Part::Cut] Cut016
  Base = -> Fillet128
  Tool = -> Fusion053
FEATURE [Part::Fillet] Fillet129  label="Fillet130"
  Base = -> Cut016
  Edges = 20 edges r=1.4: [Edge19,Edge20,Edge21,Edge22,Edge23,Edge24,Edge25,Edge26,Edge27,Edge28,Edge30,Edge31,Edge32,Edge33,Edge34,Edge35,Edge36,Edge37,Edge38,Edge39]
FEATURE [Part::MultiFuse] Fusion054  label="Top_S2"
  Placement = pos=(0,16,170) rot=(0,0,1;0rad)
  Shapes = -> [Fillet129,Chamfer034]
FEATURE [Part::Box] Box032  label="SupportBase001"
  AttacherType = Attacher::AttachEngine3D
  Height = 200
  Length = 148
  Placement = pos=(-18,0,0) rot=(0,0,1;0rad)
  Width = 4
FEATURE [Part::Box] Box033  label="Cube032"
  AttacherType = Attacher::AttachEngine3D
  Height = 80
  Length = 80
  Placement = pos=(-6.57,0,202) rot=(0,1,0;0.785398rad)
  Width = 4
FEATURE [Part::Box] Box034  label="Cube033"
  AttacherType = Attacher::AttachEngine3D
  Height = 100
  Length = 100
  Placement = pos=(-90,0,100) rot=(0,1,0;0.785398rad)
  Width = 4
FEATURE [Part::Box] Box035  label="Cube034"
  AttacherType = Attacher::AttachEngine3D
  Height = 80
  Length = 80
  Placement = pos=(-6.57,0,-2) rot=(0,1,0;0.785398rad)
  Width = 4
FEATURE [Part::Box] Box036  label="Cube035"
  AttacherType = Attacher::AttachEngine3D
  Height = 120
  Length = 120
  Placement = pos=(48.67,0,100) rot=(0,1,0;0.785398rad)
  Width = 4
FEATURE [Part::Cylinder] Cylinder089  label="ScrewHolle026"
  Angle = 360
  AttacherType = Attacher::AttachEngine3D
  FirstAngle = 0
  Height = 25
  Placement = pos=(-13,-20,15) rot=(-1,0,0;1.5708rad)
  Radius = 1.6
  SecondAngle = 0
FEATURE [Part::Cylinder] Cylinder090  label="ScrewHolle027"
  Angle = 360
  AttacherType = Attacher::AttachEngine3D
  FirstAngle = 0
  Height = 25
  Placement = pos=(125,-20,15) rot=(-1,0,0;1.5708rad)
  Radius = 1.6
  SecondAngle = 0
FEATURE [Part::Cylinder] Cylinder091  label="ScrewHolle028"
  Angle = 360
  AttacherType = Attacher::AttachEngine3D
  FirstAngle = 0
  Height = 25
  Placement = pos=(-13,-20,193) rot=(-1,0,0;1.5708rad)
  Radius = 1.6
  SecondAngle = 0
FEATURE [Part::Cylinder] Cylinder092  label="ScrewHolle029"
  Angle = 360
  AttacherType = Attacher::AttachEngine3D
  FirstAngle = 0
  Height = 25
  Placement = pos=(125,-20,193) rot=(-1,0,0;1.5708rad)
  Radius = 1.6
  SecondAngle = 0
FEATURE [Part::Fillet] Fillet130  label="Fillet131"
  Base = -> Box033
  Edges = 1 edges r=20: [Edge8]
FEATURE [Part::Fillet] Fillet131  label="Fillet132"
  Base = -> Box035
  Edges = 1 edges r=20: [Edge2]
FEATURE [Part::Fillet] Fillet132  label="Fillet133"
  Base = -> Box034
  Edges = 1 edges r=60: [Edge6]
FEATURE [Part::Fillet] Fillet133  label="Fillet134"
  Base = -> Box036
  Edges = 1 edges r=60: [Edge4]
FEATURE [Part::MultiFuse] Fusion055  label="ScrewHolles001"
  Shapes = -> [Cylinder089,Cylinder090,Cylinder091,Cylinder092]
FEATURE [Part::MultiFuse] Fusion056
  Shapes = -> [Fillet132,Fillet130,Fillet131,Fillet133,Fusion055]
FEATURE [Part::Cut] Cut017
  Base = -> Box032
  Tool = -> Fusion056
FEATURE [Part::Fillet] Fillet134  label="Fillet135"
  Base = -> Cut017
  Edges = 2 edges r=30: [Edge2,Edge67]
FEATURE [Part::Fillet] Fillet135  label="Fillet136"
  Base = -> Fillet134
  Edges = 2 edges r=10: [Edge67,Edge72]
FEATURE [Part::Chamfer] Chamfer035  label="Support2"
  Base = -> Fillet135
  Edges = 4 edges r=2: [Edge25,Edge26,Edge27,Edge28]
FEATURE [Part::Cylinder] Cylinder093
  Angle = 360
  AttacherType = Attacher::AttachEngine3D
  FirstAngle = 0
  Height = 120
  Placement = pos=(64.5,-2,2) rot=(0,0,1;0rad)
  Radius = 4.5
  SecondAngle = 0
FEATURE [Part::Fillet] Fillet136  label="Fillet137"
  Base = -> Cylinder093
  Edges = 1 edges r=4.4: [Edge2]
FEATURE [Part::Cylinder] Cylinder094
  Angle = 360
  AttacherType = Attacher::AttachEngine3D
  FirstAngle = 0
  Height = 120
  Placement = pos=(78.5,-2,2) rot=(0,0,1;0rad)
  Radius = 4.5
  SecondAngle = 0
FEATURE [Part::Fillet] Fillet137  label="Fillet138"
  Base = -> Cylinder094
  Edges = 1 edges r=4.4: [Edge2]
FEATURE [Part::Chamfer] Chamfer036
  Base = -> Box024
  Edges = 1 edges r=15: [Edge6]
FEATURE [Part::Fillet] Fillet138  label="Fillet139"
  Base = -> Chamfer036
  Edges = 1 edges r=4: [Edge15]
FEATURE [Part::Fillet] Fillet139  label="Fillet140"
  Base = -> Fillet138
  Edges = 1 edges r=9: [Edge15]
FEATURE [Part::Fillet] Fillet140  label="Fillet141"
  Base = -> Fillet139
  Edges = 1 edges r=9: [Edge15]
FEATURE [Part::MultiFuse] Fusion057
  Shapes = -> [Cylinder053,Cylinder060,Cylinder054,Fillet082,Fillet137,Fillet136,Fillet072,Fillet071,Fillet070,Fillet069,Fillet079]
FEATURE [Part::MultiFuse] Fusion058
  Shapes = -> [Fillet140,Fillet085]
FEATURE [Part::Cut] Cut018
  Base = -> Fusion058
  Tool = -> Fusion057
FEATURE [Part::MultiFuse] Fusion059  label="PencilHolder"
  Shapes = -> [Cut018,Chamfer026]
FEATURE [Part::Fillet] Fillet141  label="Fillet142"
  Base = -> Box010
  Edges = 1 edges r=10: [Edge1]
FEATURE [Part::Fillet] Fillet142  label="Fillet143"
  Base = -> Fillet141
  Edges = 1 edges r=13: [Edge4]
FEATURE [Part::MultiFuse] Fusion060
  Shapes = -> [Cylinder064,Cylinder056]
FEATURE [Part::Cut] Cut019
  Base = -> Fillet142
  Tool = -> Fusion060
FEATURE [Part::Fillet] Fillet143  label="Fillet144"
  Base = -> Cut019
  Edges = 1 edges r=15: [Edge23]
FEATURE [Part::Box] Box037  label="Cube036"
  AttacherType = Attacher::AttachEngine3D
  Height = 52
  Length = 150
  Placement = pos=(-18,8,-50) rot=(0,1,0;-0.418879rad)
  Width = 4
FEATURE [Part::Cut] Cut020
  Base = -> Box025
  Tool = -> Box037
FEATURE [Part::Fillet] Fillet144  label="Fillet145"
  Base = -> Cut020
  Edges = 1 edges r=4: [Edge4]
FEATURE [Part::Fillet] Fillet145  label="Fillet146"
  Base = -> Fillet144
  Edges = 1 edges r=8: [Edge15]
FEATURE [Part::Box] Box038  label="Cube037"
  AttacherType = Attacher::AttachEngine3D
  Height = 250
  Length = 110
  Placement = pos=(125,8,20) rot=(0,1,0;-0.541052rad)
  Width = 4
FEATURE [Part::Cut] Cut021
  Base = -> Fillet145
  Tool = -> Box038
FEATURE [Part::Fillet] Fillet146  label="Fillet147"
  Base = -> Cut021
  Edges = 1 edges r=40: [Edge8]
FEATURE [Part::Fillet] Fillet147  label="Fillet148"
  Base = -> Fillet146
  Edges = 1 edges r=20: [Edge17]
FEATURE [Part::FeaturePython] Clone  label="Fillet149"  # Draft clone (typed FeaturePython)
  AttacherType = Attacher::AttachEngine3D
  Fuse = false
  Objects = -> [Fillet147]
  Placement = pos=(9,0,30) rot=(0,0,1;0rad)
  Scale = (0.55,1,0.7)
FEATURE [Part::Cut] Cut022
  Base = -> Fillet147
  Tool = -> Clone
FEATURE [Part::MultiFuse] Fusion061
  Shapes = -> [Cylinder062,Cylinder061,Cylinder063]
FEATURE [Part::Cut] Cut023
  Base = -> Cut022
  Tool = -> Fusion061
FEATURE [Part::Chamfer] Chamfer037
  Base = -> Cut023
  Edges = 3 edges r=2: [Edge41,Edge43,Edge63]
FEATURE [Part::Fillet] Fillet148  label="Fillet150"
  Base = -> Chamfer037
  Edges = 2 edges r=3: [Edge18,Edge24]
FEATURE [Part::Chamfer] Chamfer038
  Base = -> Fillet143
  Edges = 1 edges r=2: [Edge9]
FEATURE [Part::MultiFuse] Fusion062  label="PencilHindge"
  Shapes = -> [Chamfer038,Fillet148]
FEATURE [Part::Fillet] Fillet149  label="Holder"
  Base = -> Fusion059
  Edges = 9 edges r=1.4: [Edge21,Edge26,Edge27,Edge28,Edge29,Edge30,Edge31,Edge32,Edge67]
